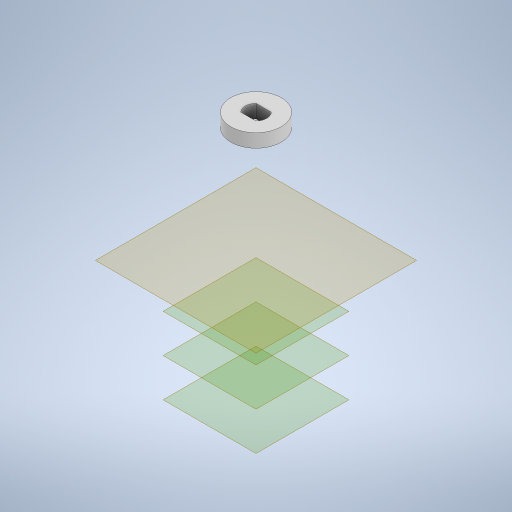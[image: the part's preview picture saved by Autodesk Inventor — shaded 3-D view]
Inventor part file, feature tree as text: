
AUTODESK INVENTOR PART (.ipt)
format: ipt  version: 2024 (Build 280153020, 153B)  size: 331,264 bytes
history: native  units: in
note: dims shown in document units (in); Inventor stores cm internally (conversion verified against a paired STEP export)
features: sketch x10, extrude x6, plane x4, loft x1, mirror x1
ambient origin geometry x8: Origin, YZ Plane, XZ Plane, XY Plane, X Axis, Y Axis, Z Axis, Center Point
bodies: Solid1 (feature_tree)
feature tree (22):
  extrude  "Extrusion1"  Depth=2.6378in TaperAngle=0.0deg
  extrude  "Extrusion2"  Depth=0.2756in TaperAngle=0.0deg
  plane  "Work Plane1"
  plane  "Work Plane2"
  sketch  "Sketch4"  dims[d6=-0.5906in d7=1.1in]
  sketch  "Sketch5"  dims[d8=0.1969in d10=-0.1969in]
  plane  "Work Plane3"
  plane  "Work Plane4"
  loft  "Loft1"
  mirror  "Mirror1"
  extrude  "Extrusion3"  [1 undecoded]
  extrude  "Extrusion4"  Depth=1.1in
  extrude  "Extrusion5"  TaperAngle=0.0deg  [1 undecoded]
  extrude  "Extrusion6"  TaperAngle=0.0deg  [1 undecoded]
  sketch  "Sketch1"  dims[d0=1.5in d1=2.6378in d2=0.0in]
  sketch  "Sketch2"  dims[d3=0.8681in d4=0.2756in d5=0.0in]
  sketch  "Sketch8"  dims[d11=0.748in d12=1.1in]
  sketch  "Sketch9"  dims[d13=0.0in d14=90.0deg d15=0.0in d16=90.0deg]
  sketch  "Sketch10"  dims[d17=0.0in d18=90.0deg d19=0.0in d20=90.0deg]
  sketch  "Sketch12"  dims[d21=0.5in d22=0.0in]
  sketch  "Sketch13"  dims[d23=0.2205in]
  sketch  "Sketch14"  dims[d24=0.0787in d25=0.0787in d26=0.3937in d27=0.0in d28=2.5in d29=0.0in d30=2.5in d31=0.0in]
note: 3 required parameter values undecoded (feature->parameter linkage not recoverable at this tier; creation-order binding heuristic only, values carry confidence <= 0.55)
